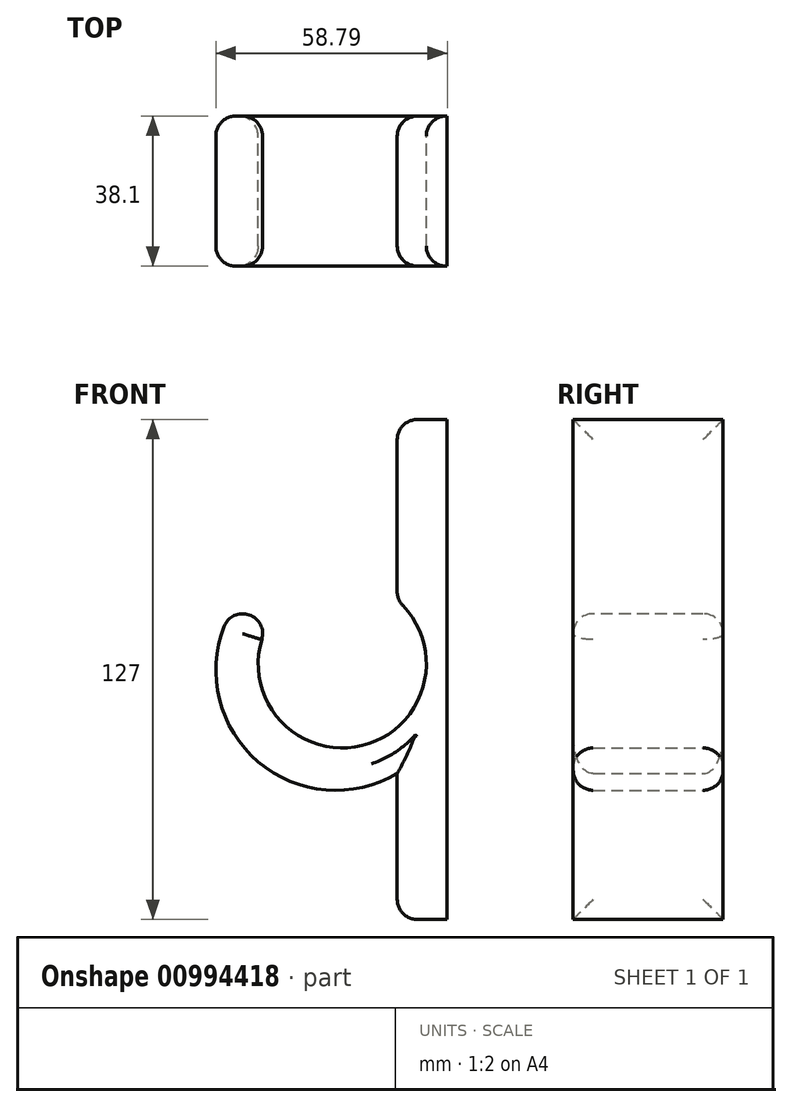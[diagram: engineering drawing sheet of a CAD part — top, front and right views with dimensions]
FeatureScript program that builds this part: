
annotation { "Feature Type Name" : "Feature", "Feature Type Description" : "" }
export const myFeature = defineFeature(function(context is Context, id is Id, definition is map)
    precondition{}
    {
        {
            var Q0;
            Q0=qCreatedBy(makeId("Front.planeOp"),FACE);
            var sketch = newSketch(context, id + "F0", { "sketchPlane" : qUnion([Q0])});
            skLineSegment(sketch, "E0.bottom", {"start": v(1.06, 73.5) * mm, "end": v(-11.64, 73.5) * mm});
            skLineSegment(sketch, "E0.top", {"start": v(1.06, -53.5) * mm, "end": v(-11.64, -53.5) * mm});
            skLineSegment(sketch, "E0.left", {"start": v(1.06, 73.5) * mm, "end": v(1.06, -53.5) * mm});
            skLineSegment(sketch, "E0.right", {"start": v(-11.64, 73.5) * mm, "end": v(-11.64, -53.5) * mm});
            skArc(sketch, "E1", {"start": v(-37.04, 29.45) * mm, "mid": v(-27.2, -9.89) * mm, "end": v(-11.64, 27.56) * mm});
            skArc(sketch, "E2", {"start": v(-46.81, 33.24) * mm, "mid": v(-52.11, -7.8) * mm, "end": v(-11.64, -16.43) * mm});
            skLineSegment(sketch, "E3", {"start": v(-46.81, 33.24) * mm, "end": v(-37.04, 29.45) * mm});
            skSolve(sketch);
        }
        {
            var Q0;
            {var subQ1=sQuery(id+"F0.wireOp",EDGE,"E0.bottom");Q0=makeQuery(id+"F0.imprint","IMPRINT",FACE,{"disambiguationData":[TD([[makeQuery(id+"F0.imprint","IMPRINT",EDGE,{"derivedFrom":subQ1}),1.0]])]});}
            var Q1;
            {var subQ0=sQuery(id+"F0.wireOp",EDGE,"E2");Q1=makeQuery(id+"F0.imprint","IMPRINT",FACE,{"disambiguationData":[TD([[makeQuery(id+"F0.imprint","IMPRINT",EDGE,{"derivedFrom":subQ0}),1.0]])]});}
            extrude(context, id + "F1", {"entities" : qUnion([Q0, Q1]), "depth" : 38.1 * mm, "offsetDistance" : 25.4 * mm});
        }
        {
            var Q0;
            Q0=makeQuery(id+"F1.opExtrude","SWEPT_EDGE",EDGE,{"disambiguationData":[OSD([sQuery(id+"F0.wireOp",EDGE,"E1"),sQuery(id+"F0.wireOp",EDGE,"E3")])]});
            fillet(context, id + "F2", {"entities" : qUnion([Q0]), "radius" : 12.7 * mm, "tangentPropagation" : true, "allowEdgeOverflow" : false});
        }
        {
            var Q0;
            Q0=makeQuery(id+"F1.opExtrude","SWEPT_EDGE",EDGE,{"disambiguationData":[OSD([sQuery(id+"F0.wireOp",EDGE,"E0.right"),sQuery(id+"F0.wireOp",EDGE,"E1")])]});
            fillet(context, id + "F3", {"entities" : qUnion([Q0]), "radius" : 5.08 * mm, "tangentPropagation" : true, "allowEdgeOverflow" : false});
        }
        {
            var Q0;
            Q0=makeQuery(id+"F1.opExtrude","SWEPT_EDGE",EDGE,{"disambiguationData":[OSD([sQuery(id+"F0.wireOp",EDGE,"E0.bottom"),sQuery(id+"F0.wireOp",EDGE,"E0.right")])]});
            var Q1;
            Q1=makeQuery(id+"F1.opExtrude","SWEPT_EDGE",EDGE,{"disambiguationData":[OSD([sQuery(id+"F0.wireOp",EDGE,"E0.top"),sQuery(id+"F0.wireOp",EDGE,"E0.right")])]});
            var Q2;
            {var subQ0=sQuery(id+"F0.wireOp",EDGE,"E0.right");Q2=makeQuery(id+"F1.opExtrude","CAP_EDGE",EDGE,{"disambiguationData":[OSD([subQ0]),TDD([makeQuery(id+"F0.imprint","IMPRINT",EDGE,{"disambiguationData":[TD([[makeQuery(id+"F0.imprint","INTERSECT",VERTEX,{"derivedFrom":[sQuery(id+"F0.wireOp",EDGE,"E0.top"),subQ0]}),1.0]])],"derivedFrom":subQ0})])],"isStart":false});}
            var Q3;
            {var subQ0=sQuery(id+"F0.wireOp",EDGE,"E0.right");Q3=makeQuery(id+"F1.opExtrude","CAP_EDGE",EDGE,{"disambiguationData":[OSD([subQ0]),TDD([makeQuery(id+"F0.imprint","IMPRINT",EDGE,{"disambiguationData":[TD([[makeQuery(id+"F0.imprint","INTERSECT",VERTEX,{"derivedFrom":[sQuery(id+"F0.wireOp",EDGE,"E0.bottom"),subQ0]}),-1.0]])],"derivedFrom":subQ0})])],"isStart":false});}
            var Q4;
            {var subQ0=sQuery(id+"F0.wireOp",EDGE,"E0.right");Q4=makeQuery(id+"F1.opExtrude","CAP_EDGE",EDGE,{"disambiguationData":[OSD([subQ0]),TDD([makeQuery(id+"F0.imprint","IMPRINT",EDGE,{"disambiguationData":[TD([[makeQuery(id+"F0.imprint","INTERSECT",VERTEX,{"derivedFrom":[sQuery(id+"F0.wireOp",EDGE,"E0.bottom"),subQ0]}),-1.0]])],"derivedFrom":subQ0})])],"isStart":true});}
            var Q5;
            {var subQ0=sQuery(id+"F0.wireOp",EDGE,"E0.right");Q5=makeQuery(id+"F1.opExtrude","CAP_EDGE",EDGE,{"disambiguationData":[OSD([subQ0]),TDD([makeQuery(id+"F0.imprint","IMPRINT",EDGE,{"disambiguationData":[TD([[makeQuery(id+"F0.imprint","INTERSECT",VERTEX,{"derivedFrom":[sQuery(id+"F0.wireOp",EDGE,"E0.top"),subQ0]}),1.0]])],"derivedFrom":subQ0})])],"isStart":true});}
            var Q6;
            Q6=makeQuery(id+"F1.opExtrude","CAP_EDGE",EDGE,{"disambiguationData":[OSD([sQuery(id+"F0.wireOp",EDGE,"E1")])],"isStart":false});
            var Q7;
            Q7=makeQuery(id+"F1.opExtrude","CAP_EDGE",EDGE,{"disambiguationData":[OSD([sQuery(id+"F0.wireOp",EDGE,"E1")])],"isStart":true});
            fillet(context, id + "F4", {"entities" : qUnion([Q0, Q1, Q2, Q3, Q4, Q5, Q6, Q7]), "radius" : 5.08 * mm, "tangentPropagation" : true, "allowEdgeOverflow" : false});
        }
        {
            var Q0;
            Q0=makeQuery(id+"F1.opExtrude","CAP_EDGE",EDGE,{"disambiguationData":[OSD([sQuery(id+"F0.wireOp",EDGE,"E2")])],"isStart":false});
            var Q1;
            Q1=makeQuery(id+"F1.opExtrude","CAP_EDGE",EDGE,{"disambiguationData":[OSD([sQuery(id+"F0.wireOp",EDGE,"E2")])],"isStart":true});
            fillet(context, id + "F5", {"entities" : qUnion([Q0, Q1]), "radius" : 5.08 * mm, "tangentPropagation" : true, "allowEdgeOverflow" : false});
        }
    });
